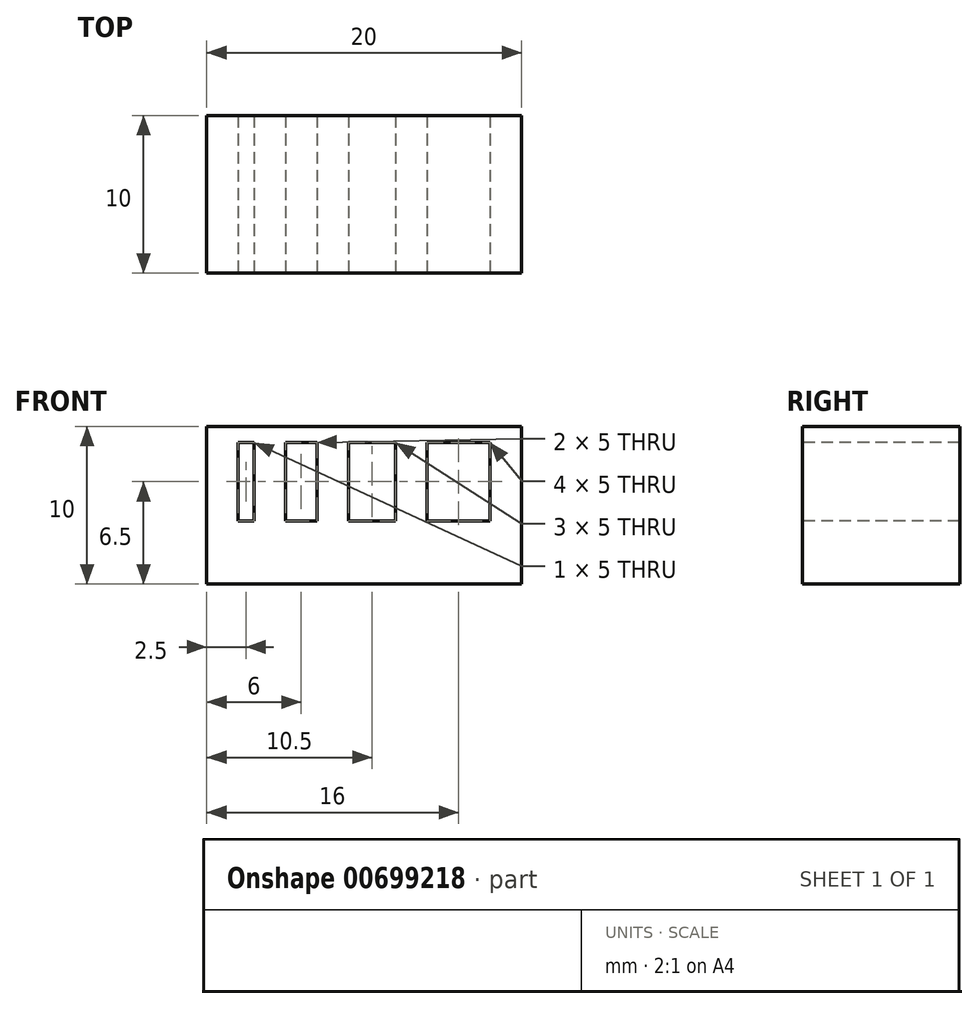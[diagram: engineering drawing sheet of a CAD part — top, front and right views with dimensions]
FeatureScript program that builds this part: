
annotation { "Feature Type Name" : "Feature", "Feature Type Description" : "" }
export const myFeature = defineFeature(function(context is Context, id is Id, definition is map)
    precondition{}
    {
        {
            var Q0;
            Q0=qCreatedBy(makeId("Top.planeOp"),FACE);
            var sketch = newSketch(context, id + "F0", { "sketchPlane" : qUnion([Q0])});
            skLineSegment(sketch, "E0.bottom", {"start": v(-10, -5) * mm, "end": v(10, -5) * mm});
            skLineSegment(sketch, "E0.top", {"start": v(-10, 5) * mm, "end": v(10, 5) * mm});
            skLineSegment(sketch, "E0.left", {"start": v(-10, -5) * mm, "end": v(-10, 5) * mm});
            skLineSegment(sketch, "E0.right", {"start": v(10, -5) * mm, "end": v(10, 5) * mm});
            skPoint(sketch, "E0.middle", {"position": v(0, 0) * mm});
            skSolve(sketch);
        }
        {
            var Q0;
            Q0=makeQuery(id+"F0.imprint","IMPRINT",FACE,{"disambiguationData":[TD([[makeQuery(id+"F0.imprint","IMPRINT",EDGE,{"derivedFrom":sQuery(id+"F0.wireOp",EDGE,"E0.bottom")}),1.0]])]});
            extrude(context, id + "F1", {"entities" : qUnion([Q0]), "depth" : 10 * mm, "offsetDistance" : 25 * mm});
        }
        {
            var Q0;
            Q0=makeQuery(id+"F1.opExtrude","SWEPT_FACE",FACE,{"disambiguationData":[OSD([sQuery(id+"F0.wireOp",EDGE,"E0.bottom")])]});
            var sketch = newSketch(context, id + "F2", { "sketchPlane" : qUnion([Q0])});
            skLineSegment(sketch, "E1.bottom", {"start": v(-8, 9) * mm, "end": v(-7, 9) * mm});
            skLineSegment(sketch, "E1.top", {"start": v(-8, 4) * mm, "end": v(-7, 4) * mm});
            skLineSegment(sketch, "E1.left", {"start": v(-8, 9) * mm, "end": v(-8, 4) * mm});
            skLineSegment(sketch, "E1.right", {"start": v(-7, 9) * mm, "end": v(-7, 4) * mm});
            skLineSegment(sketch, "E2.bottom", {"start": v(-5, 9) * mm, "end": v(-3, 9) * mm});
            skLineSegment(sketch, "E2.top", {"start": v(-5, 4) * mm, "end": v(-3, 4) * mm});
            skLineSegment(sketch, "E2.left", {"start": v(-5, 9) * mm, "end": v(-5, 4) * mm});
            skLineSegment(sketch, "E2.right", {"start": v(-3, 9) * mm, "end": v(-3, 4) * mm});
            skLineSegment(sketch, "E3.bottom", {"start": v(-1, 9) * mm, "end": v(2, 9) * mm});
            skLineSegment(sketch, "E3.top", {"start": v(-1, 4) * mm, "end": v(2, 4) * mm});
            skLineSegment(sketch, "E3.left", {"start": v(-1, 9) * mm, "end": v(-1, 4) * mm});
            skLineSegment(sketch, "E3.right", {"start": v(2, 9) * mm, "end": v(2, 4) * mm});
            skLineSegment(sketch, "E4.bottom", {"start": v(8, 9) * mm, "end": v(4, 9) * mm});
            skLineSegment(sketch, "E4.top", {"start": v(8, 4) * mm, "end": v(4, 4) * mm});
            skLineSegment(sketch, "E4.left", {"start": v(8, 9) * mm, "end": v(8, 4) * mm});
            skLineSegment(sketch, "E4.right", {"start": v(4, 9) * mm, "end": v(4, 4) * mm});
            skPoint(sketch, "E4.middle", {"position": v(6, 6.5) * mm});
            skSolve(sketch);
        }
        {
            var Q0;
            Q0=makeQuery(id+"F2.imprint","IMPRINT",FACE,{"disambiguationData":[TD([[makeQuery(id+"F2.imprint","IMPRINT",EDGE,{"derivedFrom":sQuery(id+"F2.wireOp",EDGE,"E1.bottom")}),-1.0]])]});
            var Q1;
            Q1=makeQuery(id+"F2.imprint","IMPRINT",FACE,{"disambiguationData":[TD([[makeQuery(id+"F2.imprint","IMPRINT",EDGE,{"derivedFrom":sQuery(id+"F2.wireOp",EDGE,"E2.bottom")}),-1.0]])]});
            var Q2;
            Q2=makeQuery(id+"F2.imprint","IMPRINT",FACE,{"disambiguationData":[TD([[makeQuery(id+"F2.imprint","IMPRINT",EDGE,{"derivedFrom":sQuery(id+"F2.wireOp",EDGE,"E3.bottom")}),-1.0]])]});
            var Q3;
            Q3=makeQuery(id+"F2.imprint","IMPRINT",FACE,{"disambiguationData":[TD([[makeQuery(id+"F2.imprint","IMPRINT",EDGE,{"derivedFrom":sQuery(id+"F2.wireOp",EDGE,"E4.bottom")}),1.0]])]});
            extrude(context, id + "F3", {"entities" : qUnion([Q0, Q1, Q2, Q3]), "operationType" : NewBodyOperationType.REMOVE, "endBound" : BoundingType.THROUGH_ALL, "oppositeDirection" : true, "depth" : 25 * mm, "offsetDistance" : 25 * mm});
        }
    });
